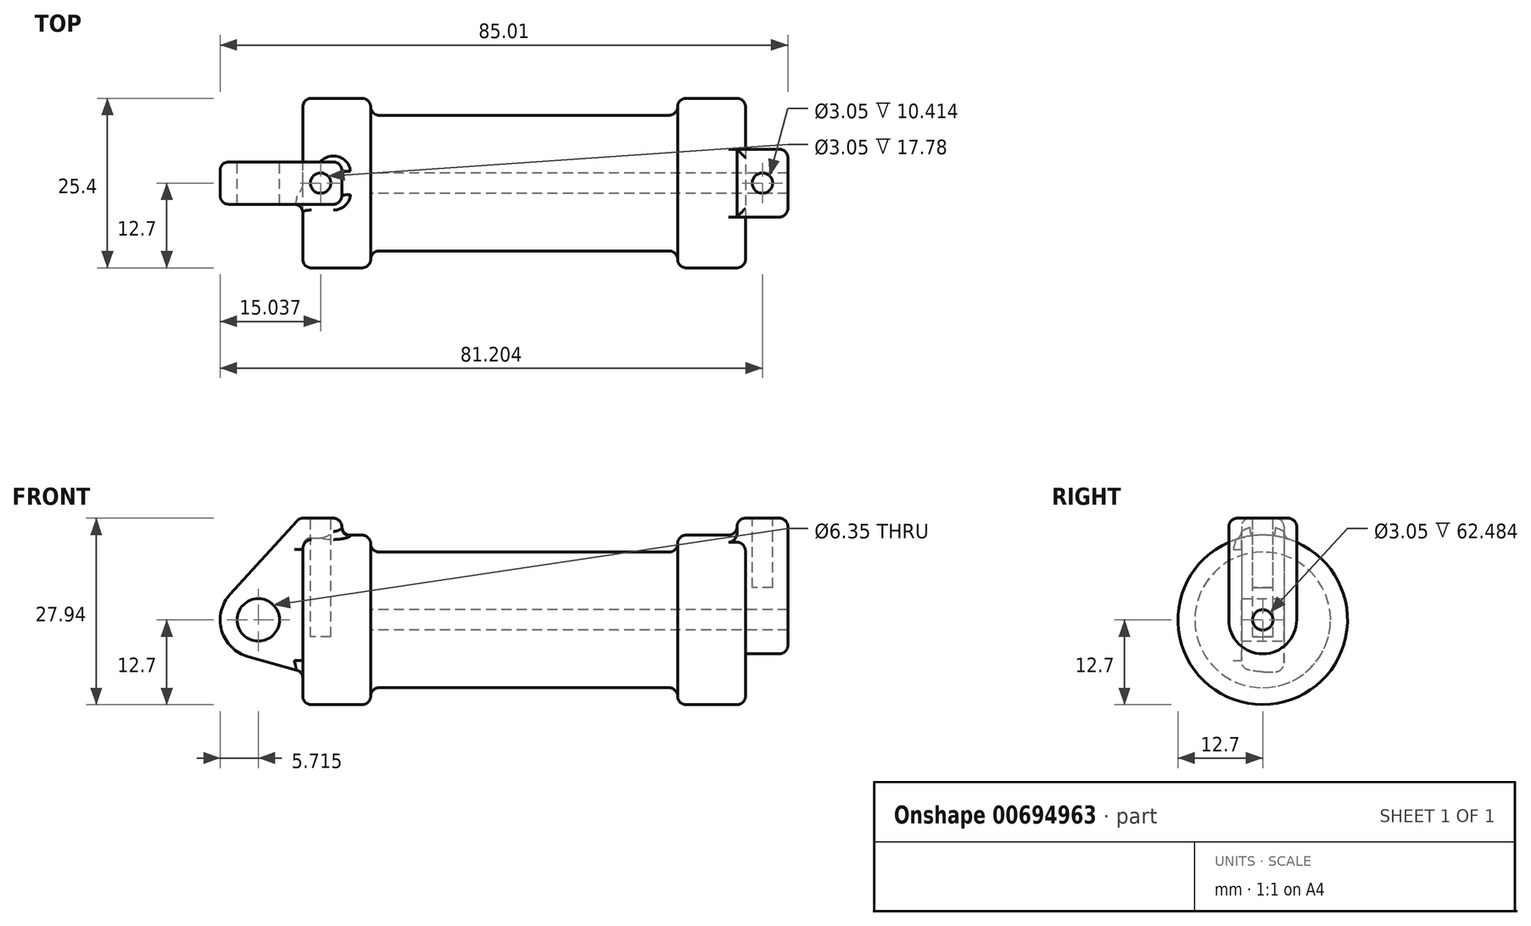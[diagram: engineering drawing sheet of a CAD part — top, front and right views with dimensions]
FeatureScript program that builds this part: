
annotation { "Feature Type Name" : "Feature", "Feature Type Description" : "" }
export const myFeature = defineFeature(function(context is Context, id is Id, definition is map)
    precondition{}
    {
        {
            var Q0;
            Q0=qCreatedBy(makeId("Front.planeOp"),FACE);
            var sketch = newSketch(context, id + "F0", { "sketchPlane" : qUnion([Q0])});
            skLineSegment(sketch, "E0", {"start": v(0, 0) * mm, "end": v(0, 12.7) * mm});
            skLineSegment(sketch, "E1", {"start": v(0, 12.7) * mm, "end": v(10.16, 12.7) * mm});
            skLineSegment(sketch, "E2", {"start": v(10.16, 12.7) * mm, "end": v(10.16, 10.16) * mm});
            skLineSegment(sketch, "E3", {"start": v(10.16, 10.16) * mm, "end": v(56.13, 10.16) * mm});
            skLineSegment(sketch, "E4", {"start": v(56.13, 10.16) * mm, "end": v(56.13, 12.7) * mm});
            skLineSegment(sketch, "E5", {"start": v(56.13, 12.7) * mm, "end": v(66.3, 12.7) * mm});
            skLineSegment(sketch, "E6", {"start": v(66.3, 12.7) * mm, "end": v(66.3, 0) * mm});
            skLineSegment(sketch, "E7", {"start": v(66.3, 0) * mm, "end": v(0, 0) * mm});
            skLineSegment(sketch, "E8", {"start": v(5.84, 15.24) * mm, "end": v(-0.5, 15.24) * mm});
            skLineSegment(sketch, "E9", {"start": v(-0.5, 15.24) * mm, "end": v(-10.88, 3.85) * mm});
            skLineSegment(sketch, "E10", {"start": v(0, 0) * mm, "end": v(-6.65, 0) * mm});
            skCircle(sketch, "E11", {"center": v(-6.65, 0) * mm, "radius": 5.72 * mm});
            skCircle(sketch, "E12", {"center": v(-6.65, 0) * mm, "radius": 3.18 * mm});
            skLineSegment(sketch, "E13", {"start": v(5.84, 15.24) * mm, "end": v(5.84, -9.4) * mm});
            skLineSegment(sketch, "E14", {"start": v(5.84, -9.4) * mm, "end": v(-8.18, -5.5) * mm});
            skSolve(sketch);
        }
        {
            var Q0;
            {var subQ0=sQuery(id+"F0.wireOp",EDGE,"E2");Q0=makeQuery(id+"F0.imprint","IMPRINT",FACE,{"disambiguationData":[TD([[makeQuery(id+"F0.imprint","IMPRINT",EDGE,{"derivedFrom":subQ0}),-1.0]])]});}
            var Q1;
            {var subQ0=sQuery(id+"F0.wireOp",EDGE,"E0");Q1=makeQuery(id+"F0.imprint","IMPRINT",FACE,{"disambiguationData":[TD([[makeQuery(id+"F0.imprint","IMPRINT",EDGE,{"derivedFrom":subQ0}),-1.0]])]});}
            var Q2;
            Q2=sQuery(id+"F0.wireOp",EDGE,"E7");
            revolve(context, id + "F1", {"entities" : qUnion([Q0, Q1]), "axis" : qUnion([Q2]), "revolveType" : RevolveType.FULL});
        }
        {
            var Q0;
            {var subQ0=sQuery(id+"F0.wireOp",EDGE,"E0");Q0=makeQuery(id+"F0.imprint","IMPRINT",FACE,{"disambiguationData":[TD([[makeQuery(id+"F0.imprint","IMPRINT",EDGE,{"derivedFrom":subQ0}),-1.0]])]});}
            var Q1;
            {var subQ1=sQuery(id+"F0.wireOp",EDGE,"E0");Q1=makeQuery(id+"F0.imprint","IMPRINT",FACE,{"disambiguationData":[TD([[makeQuery(id+"F0.imprint","IMPRINT",EDGE,{"derivedFrom":subQ1}),1.0]])]});}
            var Q2;
            {var subQ5=sQuery(id+"F0.wireOp",EDGE,"E12");Q2=makeQuery(id+"F0.imprint","IMPRINT",FACE,{"disambiguationData":[TD([[makeQuery(id+"F0.imprint","IMPRINT",EDGE,{"derivedFrom":subQ5}),-1.0]])]});}
            var Q3;
            {var subQ0=sQuery(id+"F0.wireOp",EDGE,"E14");Q3=makeQuery(id+"F0.imprint","IMPRINT",FACE,{"disambiguationData":[TD([[makeQuery(id+"F0.imprint","IMPRINT",EDGE,{"derivedFrom":subQ0}),-1.0]])]});}
            var Q4;
            Q4=makeQuery(id+"F1.opRevolve","SWEPT_BODY",BODY,{"disambiguationData":[OSD([sQuery(id+"F0.wireOp",EDGE,"E0"),sQuery(id+"F0.wireOp",EDGE,"E1"),sQuery(id+"F0.wireOp",EDGE,"E2"),sQuery(id+"F0.wireOp",EDGE,"E3"),sQuery(id+"F0.wireOp",EDGE,"E4"),sQuery(id+"F0.wireOp",EDGE,"E5"),sQuery(id+"F0.wireOp",EDGE,"E6"),sQuery(id+"F0.wireOp",EDGE,"E7")])]});
            extrude(context, id + "F2", {"entities" : qUnion([Q0, Q1, Q2, Q3]), "operationType" : NewBodyOperationType.ADD, "depth" : 6.35 * mm, "endBoundEntityBody" : qUnion([Q4]), "offsetDistance" : 25.4 * mm, "symmetric" : true});
        }
        {
            var Q0;
            Q0=makeQuery(id+"F1.opRevolve","SWEPT_FACE",FACE,{"disambiguationData":[OSD([sQuery(id+"F0.wireOp",EDGE,"E6")])]});
            var sketch = newSketch(context, id + "F3", { "sketchPlane" : qUnion([Q0])});
            skCircle(sketch, "E15", {"center": v(0, 0) * mm, "radius": 1.52 * mm});
            skCircle(sketch, "E16", {"center": v(0, 0) * mm, "radius": 5.08 * mm});
            skLineSegment(sketch, "E17", {"start": v(5.08, 0) * mm, "end": v(5.08, 15.24) * mm});
            skLineSegment(sketch, "E18", {"start": v(5.08, 15.24) * mm, "end": v(-5.08, 15.24) * mm});
            skLineSegment(sketch, "E19", {"start": v(-5.08, 15.24) * mm, "end": v(-5.08, 0) * mm});
            skSolve(sketch);
        }
        {
            var Q0;
            Q0 = qSketchRegion(id + "F3", true);
            var Q1;
            Q1=makeQuery(id+"F1.opRevolve","SWEPT_BODY",BODY,{"disambiguationData":[OSD([sQuery(id+"F0.wireOp",EDGE,"E0"),sQuery(id+"F0.wireOp",EDGE,"E1"),sQuery(id+"F0.wireOp",EDGE,"E2"),sQuery(id+"F0.wireOp",EDGE,"E3"),sQuery(id+"F0.wireOp",EDGE,"E4"),sQuery(id+"F0.wireOp",EDGE,"E5"),sQuery(id+"F0.wireOp",EDGE,"E6"),sQuery(id+"F0.wireOp",EDGE,"E7")])]});
            extrude(context, id + "F4", {"entities" : qUnion([Q0]), "operationType" : NewBodyOperationType.ADD, "depth" : 6.35 * mm, "endBoundEntityBody" : qUnion([Q1]), "offsetDistance" : 25.4 * mm});
        }
        {
            var Q0;
            Q0 = qSketchRegion(id + "F3", true);
            extrude(context, id + "F5", {"entities" : qUnion([Q0]), "operationType" : NewBodyOperationType.ADD, "oppositeDirection" : true, "depth" : 1.27 * mm, "offsetDistance" : 25.4 * mm});
        }
        {
            var Q0;
            Q0=makeQuery(id+"F4.boolean.opBoolean","SPLIT",FACE,{"disambiguationData":[TD([makeQuery(id+"F4.opExtrude","SWEPT_FACE",FACE,{"disambiguationData":[OSD([sQuery(id+"F3.wireOp",EDGE,"E15")])]})])],"derivedFrom":makeQuery(id+"F1.opRevolve","SWEPT_FACE",FACE,{"disambiguationData":[OSD([sQuery(id+"F0.wireOp",EDGE,"E6")])]})});
            var Q1;
            Q1=makeQuery(id+"F1.opRevolve","SWEPT_FACE",FACE,{"disambiguationData":[OSD([sQuery(id+"F0.wireOp",EDGE,"E2")])]});
            extrude(context, id + "F6", {"entities" : qUnion([Q0]), "operationType" : NewBodyOperationType.REMOVE, "endBound" : BoundingType.UP_TO_SURFACE, "oppositeDirection" : true, "depth" : 25.4 * mm, "endBoundEntityFace" : qUnion([Q1]), "offsetDistance" : 25.4 * mm});
        }
        {
            var Q0;
            Q0=makeQuery(id+"F2.opExtrude","SWEPT_FACE",FACE,{"disambiguationData":[OSD([sQuery(id+"F0.wireOp",EDGE,"E8")])]});
            var sketch = newSketch(context, id + "F7", { "sketchPlane" : qUnion([Q0])});
            skCircle(sketch, "E20", {"center": v(2.67, 0) * mm, "radius": 1.52 * mm});
            skSolve(sketch);
        }
        {
            var Q0;
            {var subQ0=sQuery(id+"F3.wireOp",EDGE,"E18");Q0=makeQuery(id+"F5.boolean.opBoolean","MERGE",FACE,{"derivedFrom":[makeQuery(id+"F4.opExtrude","SWEPT_FACE",FACE,{"disambiguationData":[OSD([subQ0])]}),makeQuery(id+"F5.opExtrude","SWEPT_FACE",FACE,{"disambiguationData":[OSD([subQ0])]})]});}
            var sketch = newSketch(context, id + "F8", { "sketchPlane" : qUnion([Q0])});
            skCircle(sketch, "E21", {"center": v(68.83, 0) * mm, "radius": 1.52 * mm});
            skSolve(sketch);
        }
        {
            var Q0;
            Q0 = qSketchRegion(id + "F8", true);
            extrude(context, id + "F9", {"entities" : qUnion([Q0]), "operationType" : NewBodyOperationType.REMOVE, "oppositeDirection" : true, "depth" : 10.4 * mm, "offsetDistance" : 25.4 * mm});
        }
        {
            var Q0;
            Q0 = qSketchRegion(id + "F7", true);
            extrude(context, id + "F10", {"entities" : qUnion([Q0]), "operationType" : NewBodyOperationType.REMOVE, "oppositeDirection" : true, "depth" : 17.78 * mm, "offsetDistance" : 25.4 * mm});
        }
        {
            var Q0;
            Q0=makeQuery(id+"F1.opRevolve","SWEPT_EDGE",EDGE,{"disambiguationData":[OSD([sQuery(id+"F0.wireOp",EDGE,"E1"),sQuery(id+"F0.wireOp",EDGE,"E2")])]});
            var Q1;
            Q1=makeQuery(id+"F1.opRevolve","SWEPT_EDGE",EDGE,{"disambiguationData":[OSD([sQuery(id+"F0.wireOp",EDGE,"E2"),sQuery(id+"F0.wireOp",EDGE,"E3")])]});
            var Q2;
            {var subQ0=sQuery(id+"F0.wireOp",EDGE,"E5");var subQ1=sQuery(id+"F0.wireOp",EDGE,"E6");Q2=makeQuery(id+"F4.boolean.opBoolean","SPLIT",EDGE,{"disambiguationData":[topologyDisambiguationEdgeConnected([makeQuery(id+"F1.opRevolve","SWEPT_FACE",FACE,{"disambiguationData":[OSD([subQ1])]})])],"derivedFrom":makeQuery(id+"F1.opRevolve","SWEPT_EDGE",EDGE,{"disambiguationData":[OSD([subQ0,subQ1])]})});}
            var Q3;
            Q3=makeQuery(id+"F1.opRevolve","SWEPT_EDGE",EDGE,{"disambiguationData":[OSD([sQuery(id+"F0.wireOp",EDGE,"E4"),sQuery(id+"F0.wireOp",EDGE,"E5")])]});
            var Q4;
            Q4=makeQuery(id+"F1.opRevolve","SWEPT_EDGE",EDGE,{"disambiguationData":[OSD([sQuery(id+"F0.wireOp",EDGE,"E3"),sQuery(id+"F0.wireOp",EDGE,"E4")])]});
            var Q5;
            Q5=makeQuery(id+"F1.opRevolve","SWEPT_EDGE",EDGE,{"disambiguationData":[OSD([sQuery(id+"F0.wireOp",EDGE,"E0"),sQuery(id+"F0.wireOp",EDGE,"E1")])]});
            fillet(context, id + "F11", {"entities" : qUnion([Q0, Q1, Q2, Q3, Q4, Q5]), "radius" : 1.27 * mm, "tangentPropagation" : true, "allowEdgeOverflow" : false});
        }
        {
            var Q0;
            Q0=makeQuery(id+"F4.opExtrude","CAP_EDGE",EDGE,{"disambiguationData":[OSD([sQuery(id+"F3.wireOp",EDGE,"E17")])],"isStart":false});
            var Q1;
            {var subQ0=sQuery(id+"F3.wireOp",EDGE,"E17");Q1=makeQuery(id+"F4.boolean.opBoolean","SPLIT",EDGE,{"disambiguationData":[topologyDisambiguationEdgeConnected([makeQuery(id+"F1.opRevolve","SWEPT_FACE",FACE,{"disambiguationData":[OSD([sQuery(id+"F0.wireOp",EDGE,"E6")])]})])],"derivedFrom":makeQuery(id+"F4.opExtrude","CAP_EDGE",EDGE,{"disambiguationData":[OSD([subQ0])],"isStart":true})});}
            var Q2;
            Q2=makeQuery(id+"F4.opExtrude","CAP_EDGE",EDGE,{"disambiguationData":[OSD([sQuery(id+"F3.wireOp",EDGE,"E18")])],"isStart":false});
            var Q3;
            {var subQ0=sQuery(id+"F3.wireOp",EDGE,"E19");var subQ1=sQuery(id+"F3.wireOp",EDGE,"E18");Q3=makeQuery(id+"F5.boolean.opBoolean","MERGE",EDGE,{"derivedFrom":[makeQuery(id+"F4.opExtrude","SWEPT_EDGE",EDGE,{"disambiguationData":[OSD([subQ1,subQ0])]}),makeQuery(id+"F5.opExtrude","SWEPT_EDGE",EDGE,{"disambiguationData":[OSD([subQ1,subQ0])]})]});}
            var Q4;
            Q4=makeQuery(id+"F5.opExtrude","CAP_EDGE",EDGE,{"disambiguationData":[OSD([sQuery(id+"F3.wireOp",EDGE,"E18")])],"isStart":false});
            var Q5;
            {var subQ0=sQuery(id+"F3.wireOp",EDGE,"E18");var subQ1=sQuery(id+"F3.wireOp",EDGE,"E17");Q5=makeQuery(id+"F5.boolean.opBoolean","MERGE",EDGE,{"derivedFrom":[makeQuery(id+"F4.opExtrude","SWEPT_EDGE",EDGE,{"disambiguationData":[OSD([subQ1,subQ0])]}),makeQuery(id+"F5.opExtrude","SWEPT_EDGE",EDGE,{"disambiguationData":[OSD([subQ1,subQ0])]})]});}
            var Q6;
            Q6=makeQuery(id+"F5.boolean.opBoolean","INTERSECT",EDGE,{"derivedFrom":[makeQuery(id+"F1.opRevolve","SWEPT_FACE",FACE,{"disambiguationData":[OSD([sQuery(id+"F0.wireOp",EDGE,"E5")])]}),makeQuery(id+"F5.opExtrude","CAP_FACE",FACE,{"disambiguationData":[OSD([sQuery(id+"F3.wireOp",EDGE,"E15"),sQuery(id+"F3.wireOp",EDGE,"E16"),sQuery(id+"F3.wireOp",EDGE,"E17"),sQuery(id+"F3.wireOp",EDGE,"E18"),sQuery(id+"F3.wireOp",EDGE,"E19")])],"isStart":false})]});
            fillet(context, id + "F12", {"entities" : qUnion([Q0, Q1, Q2, Q3, Q4, Q5, Q6]), "radius" : 1.27 * mm, "tangentPropagation" : true, "allowEdgeOverflow" : false});
        }
        {
            var Q0;
            Q0=makeQuery(id+"F2.opExtrude","CAP_EDGE",EDGE,{"disambiguationData":[OSD([sQuery(id+"F0.wireOp",EDGE,"E9")])],"isStart":false});
            var Q1;
            Q1=makeQuery(id+"F2.opExtrude","CAP_EDGE",EDGE,{"disambiguationData":[OSD([sQuery(id+"F0.wireOp",EDGE,"E9")])],"isStart":true});
            var Q2;
            Q2=makeQuery(id+"F2.opExtrude","CAP_EDGE",EDGE,{"disambiguationData":[OSD([sQuery(id+"F0.wireOp",EDGE,"E8")])],"isStart":false});
            var Q3;
            Q3=makeQuery(id+"F2.boolean.opBoolean","INTERSECT",EDGE,{"derivedFrom":[makeQuery(id+"F1.opRevolve","SWEPT_FACE",FACE,{"disambiguationData":[OSD([sQuery(id+"F0.wireOp",EDGE,"E0")])]}),makeQuery(id+"F2.opExtrude","CAP_FACE",FACE,{"disambiguationData":[OSD([sQuery(id+"F0.wireOp",EDGE,"E8"),sQuery(id+"F0.wireOp",EDGE,"E9"),sQuery(id+"F0.wireOp",EDGE,"E11"),sQuery(id+"F0.wireOp",EDGE,"E12"),sQuery(id+"F0.wireOp",EDGE,"E13"),sQuery(id+"F0.wireOp",EDGE,"E14")])],"isStart":false})]});
            var Q4;
            Q4=makeQuery(id+"F2.opExtrude","CAP_EDGE",EDGE,{"disambiguationData":[OSD([sQuery(id+"F0.wireOp",EDGE,"E8")])],"isStart":true});
            var Q5;
            Q5=makeQuery(id+"F2.opExtrude","SWEPT_EDGE",EDGE,{"disambiguationData":[OSD([sQuery(id+"F0.wireOp",EDGE,"E8"),sQuery(id+"F0.wireOp",EDGE,"E13")])]});
            var Q6;
            Q6=makeQuery(id+"F2.boolean.opBoolean","INTERSECT",EDGE,{"derivedFrom":[makeQuery(id+"F1.opRevolve","SWEPT_FACE",FACE,{"disambiguationData":[OSD([sQuery(id+"F0.wireOp",EDGE,"E1")])]}),makeQuery(id+"F2.opExtrude","SWEPT_FACE",FACE,{"disambiguationData":[OSD([sQuery(id+"F0.wireOp",EDGE,"E13")])]})]});
            var Q7;
            Q7=makeQuery(id+"F2.opExtrude","CAP_EDGE",EDGE,{"disambiguationData":[OSD([sQuery(id+"F0.wireOp",EDGE,"E13")])],"isStart":false});
            var Q8;
            Q8=makeQuery(id+"F2.opExtrude","CAP_EDGE",EDGE,{"disambiguationData":[OSD([sQuery(id+"F0.wireOp",EDGE,"E13")])],"isStart":true});
            var Q9;
            Q9=makeQuery(id+"F2.opExtrude","SWEPT_EDGE",EDGE,{"disambiguationData":[OSD([sQuery(id+"F0.wireOp",EDGE,"E8"),sQuery(id+"F0.wireOp",EDGE,"E9")])]});
            fillet(context, id + "F13", {"entities" : qUnion([Q0, Q1, Q2, Q3, Q4, Q5, Q6, Q7, Q8, Q9]), "radius" : 1.27 * mm, "tangentPropagation" : true, "allowEdgeOverflow" : false});
        }
    });
